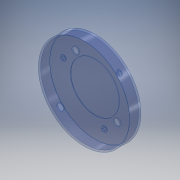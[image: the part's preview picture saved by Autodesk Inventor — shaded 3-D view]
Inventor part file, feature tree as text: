
AUTODESK INVENTOR PART (.ipt)
format: ipt  version: 2018 (Build 220112000, 112)  size: 312,832 bytes
history: native  units: mm
features: extrude x6, sketch x6, pattern_circular x2, shell x1
ambient origin geometry x8: Origin, YZ Plane, XZ Plane, XY Plane, X Axis, Y Axis, Z Axis, Center Point
bodies: 实体1 (feature_tree)
feature tree (15):
  extrude  "拉伸1"  Depth=17.0mm TaperAngle=0.0deg
  extrude  "拉伸3"  Depth=8.0mm
  shell  "抽壳1"  Thickness=35.0mm
  extrude  "拉伸5"  Depth=1.0mm TaperAngle=0.0deg
  extrude  "拉伸6"  Depth=1.8mm
  pattern_circular  "环形阵列1"  Count=5  [1 undecoded]
  extrude  "拉伸7"  Depth=2.0mm TaperAngle=0.0deg
  extrude  "拉伸8"  Depth=4.0mm TaperAngle=360.0deg
  pattern_circular  "环形阵列2"  [2 undecoded]
  sketch  "草图1"  dims[d0=135.0mm d1=17.0mm d2=0.0mm]
  sketch  "草图3"  dims[d3=100.0mm d8=8.0mm d9=35.0mm]
  sketch  "草图6"  dims[d10=35.0mm d11=1.0mm d12=0.0mm]
  sketch  "草图7"  dims[d13=1.8mm d17=72.0mm]
  sketch  "草图8"  dims[d18=1.0mm d19=0.0mm]
  sketch  "草图9"  dims[d25=10.0mm d26=50.0mm d27=2.0mm d28=0.0mm d29=30.0mm d30=360.0deg d32=4.0mm d33=3.0mm d34=0.0mm d35=4.0mm d36=3.0mm d37=0.0mm d39=30.0mm d40=360.0deg d42=60.0deg]
note: 3 required parameter values undecoded (feature->parameter linkage not recoverable at this tier; creation-order binding heuristic only, values carry confidence <= 0.55)
